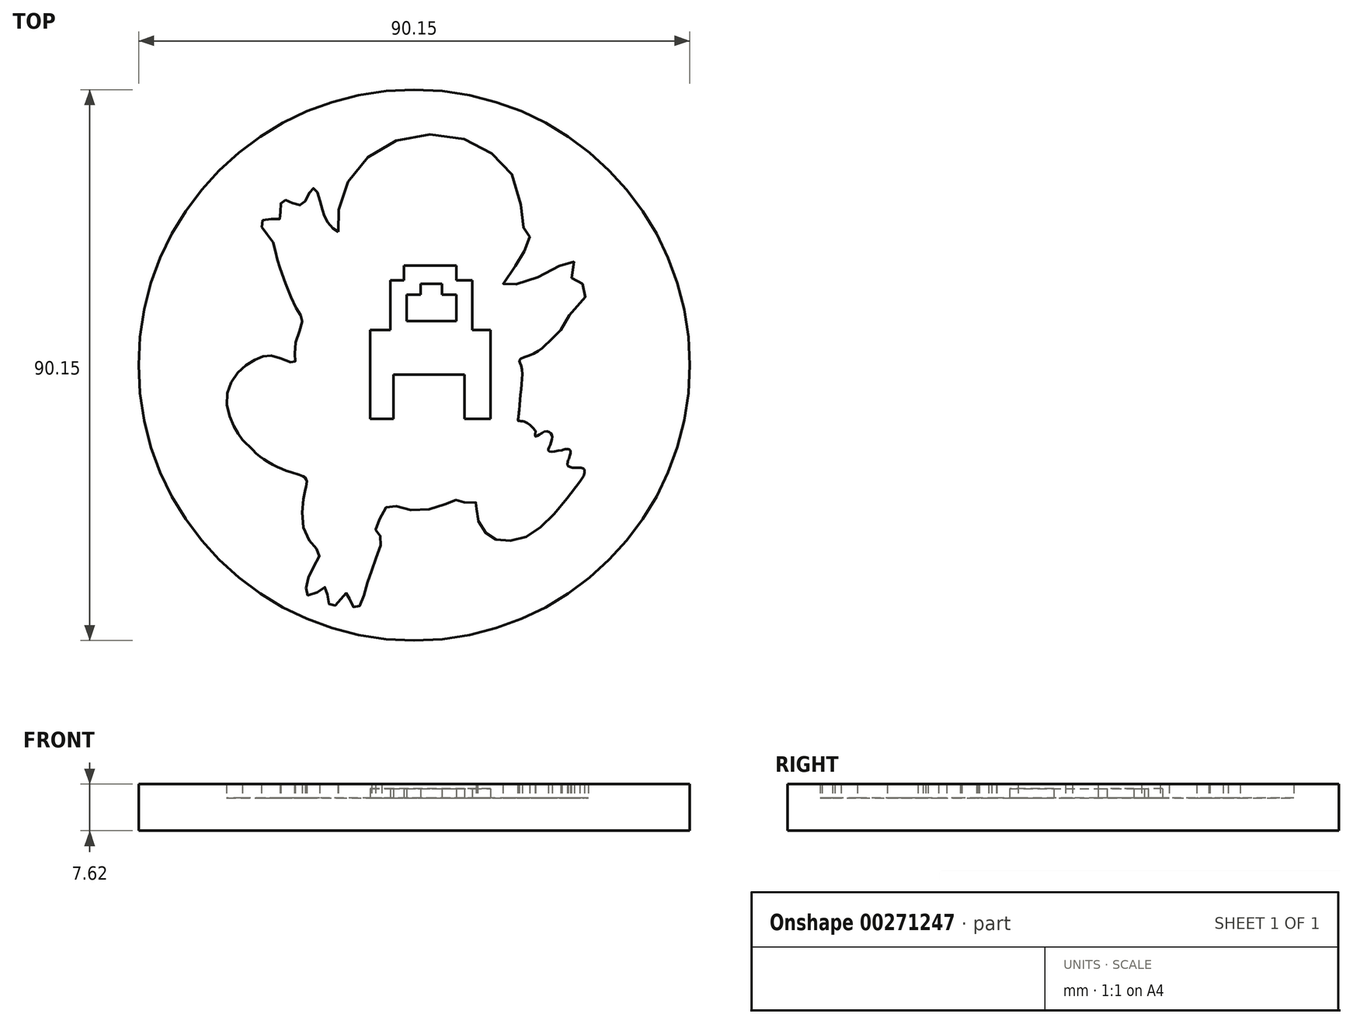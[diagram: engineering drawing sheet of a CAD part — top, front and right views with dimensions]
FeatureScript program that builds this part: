
annotation { "Feature Type Name" : "Feature", "Feature Type Description" : "" }
export const myFeature = defineFeature(function(context is Context, id is Id, definition is map)
    precondition{}
    {
        {
            var Q0;
            Q0=qCreatedBy(makeId("Top.planeOp"),FACE);
            var sketch = newSketch(context, id + "F0", { "sketchPlane" : qUnion([Q0])});
            skFitSpline(sketch, "E0", {"points": [v(-19.32, 16.1) * mm, v(-19.32, 19.22) * mm, v(-17.52, 24.62) * mm, v(-12.85, 29.53) * mm, v(-5.66, 31.93) * mm, v(2.13, 30.97) * mm, v(7.29, 27.61) * mm, v(10.28, 22.58) * mm, v(10.76, 17.07) * mm, v(11.2, 16.56) * mm, v(11.82, 15.85) * mm, v(11.96, 14.7) * mm, v(11.23, 13.16) * mm, v(10.25, 11.43) * mm, v(8.9, 9.4) * mm, v(7.6, 7.25) * mm, v(8.95, 7.25) * mm, v(12.21, 8.36) * mm, v(15.6, 9.53) * mm, v(18.49, 11.62) * mm, v(19.29, 10.94) * mm, v(18.92, 9.1) * mm, v(18.98, 7.87) * mm, v(20.52, 7.62) * mm, v(21.56, 6.4) * mm, v(19.9, 4.24) * mm, v(17.69, 1.29) * mm, v(17.07, 0) * mm], "startDerivative": vector(-5.64, 75.27) * mm, "endDerivative": vector(-18.44, -44.4) * mm});
            skFitSpline(sketch, "E1", {"points": [v(17.07, 0) * mm, v(15.3, -1.73) * mm, v(12.65, -3.84) * mm, v(10.32, -4.93) * mm, v(10.63, -5.94) * mm, v(10.63, -9.13) * mm, v(10.24, -13.1) * mm], "startDerivative": vector(-10.72, -10.36) * mm, "endDerivative": vector(-1.84, -19.44) * mm});
            skFitSpline(sketch, "E2", {"points": [v(10.24, -13.1) * mm, v(10.09, -14.52) * mm, v(10.05, -14.77) * mm, v(10.84, -14.93) * mm, v(12.08, -15.58) * mm, v(12.83, -16.38) * mm, v(12.96, -16.64) * mm], "startDerivative": vector(-0.46, -7.58) * mm, "endDerivative": vector(0.85, -2.32) * mm});
            skFitSpline(sketch, "E3", {"points": [v(12.96, -16.64) * mm, v(12.96, -17.44) * mm, v(14.36, -16.64) * mm, v(15.54, -17.04) * mm, v(15.37, -18.62) * mm, v(15.06, -19.77) * mm, v(17.23, -19.63) * mm], "startDerivative": vector(-1.66, -9.1) * mm, "endDerivative": vector(14.16, 2.9) * mm});
            skFitSpline(sketch, "E4", {"points": [v(17.23, -19.63) * mm, v(18.1, -19.46) * mm, v(18.65, -19.8) * mm, v(18.4, -20.98) * mm, v(18.15, -22) * mm, v(18.3, -22.28) * mm], "startDerivative": vector(4.13, 1.41) * mm, "endDerivative": vector(1.55, -1.87) * mm});
            skFitSpline(sketch, "E5", {"points": [v(18.3, -22.28) * mm, v(18.91, -22.51) * mm, v(20.12, -22.54) * mm, v(20.87, -22.76) * mm, v(20.79, -23.83) * mm, v(20.14, -24.8) * mm], "startDerivative": vector(3.33, -1.69) * mm, "endDerivative": vector(-3.28, -4) * mm});
            skFitSpline(sketch, "E6", {"points": [v(20.14, -24.8) * mm, v(15.28, -30.83) * mm, v(10.63, -34.1) * mm, v(6.5, -34.27) * mm, v(4.25, -32.55) * mm, v(3.22, -29.45) * mm, v(3.4, -28.33) * mm, v(1.24, -28.16) * mm, v(0, -27.82) * mm, v(-2.72, -28.85) * mm, v(-8.4, -29.28) * mm, v(-11.16, -28.76) * mm, v(-12.8, -31.43) * mm, v(-13.14, -32.98) * mm, v(-12.28, -33.93) * mm, v(-12.8, -36.25) * mm, v(-13.83, -39.35) * mm], "startDerivative": vector(-47.35, -63.76) * mm, "endDerivative": vector(-14.46, -47.3) * mm});
            skFitSpline(sketch, "E7", {"points": [v(-13.83, -39.35) * mm, v(-14.94, -42.61) * mm, v(-15.9, -45.2) * mm, v(-16.78, -45.37) * mm, v(-17.48, -43.97) * mm, v(-17.96, -43.05) * mm, v(-18.7, -43.67) * mm, v(-19.71, -44.98) * mm, v(-20.67, -45.02) * mm, v(-21.07, -43.53) * mm, v(-21.46, -42.09) * mm, v(-22.78, -42.92) * mm, v(-24.53, -43.32) * mm, v(-24.49, -41.65) * mm, v(-23.7, -39.35) * mm, v(-22.38, -36.7) * mm, v(-23.22, -35.47) * mm, v(-24.97, -32.55) * mm, v(-25.1, -28.16) * mm, v(-24.75, -26.1) * mm], "startDerivative": vector(-16.81, -44.88) * mm, "endDerivative": vector(6.7, 32.94) * mm});
            skFitSpline(sketch, "E8", {"points": [v(-24.75, -26.1) * mm, v(-24.53, -24.51) * mm, v(-25.28, -23.83) * mm, v(-26.5, -23.46) * mm, v(-31.08, -21.45) * mm, v(-34.98, -17.92) * mm], "startDerivative": vector(3.32, 11.18) * mm, "endDerivative": vector(-13.1, 13.12) * mm});
            skFitSpline(sketch, "E9", {"points": [v(-34.98, -17.92) * mm, v(-36.3, -15.94) * mm, v(-37.58, -11.32) * mm, v(-35.6, -6.77) * mm, v(-32.18, -4.5) * mm, v(-29.56, -4.36) * mm, v(-26.5, -5.28) * mm, v(-26.5, -3.06) * mm, v(-25.23, 1.5) * mm, v(-26.01, 3.23) * mm, v(-28.88, 10.14) * mm], "startDerivative": vector(-16.02, 21.1) * mm, "endDerivative": vector(-20.54, 57.47) * mm});
            skFitSpline(sketch, "E10", {"points": [v(-28.88, 10.14) * mm, v(-29.5, 12.4) * mm, v(-30.28, 14.88) * mm, v(-31.86, 16.96) * mm, v(-31.37, 18.19) * mm, v(-28.88, 18.19) * mm, v(-28.88, 20.04) * mm, v(-28.2, 21.27) * mm, v(-26.7, 20.77) * mm, v(-25.2, 20.54) * mm, v(-24.17, 22.3) * mm, v(-23.3, 23.21) * mm, v(-22.54, 21.95) * mm, v(-21.9, 19.6) * mm, v(-21.45, 18.32) * mm, v(-20.4, 16.83) * mm, v(-19.32, 16.1) * mm], "startDerivative": vector(-9.75, 30.83) * mm, "endDerivative": vector(20.83, -10.87) * mm});
            skCircle(sketch, "E11", {"center": v(-6.92, -5.72) * mm, "radius": 45.07 * mm});
            skSolve(sketch);
        }
        {
            var Q0;
            Q0=makeQuery(id+"F0.imprint","IMPRINT",FACE,{"disambiguationData":[TD([[makeQuery(id+"F0.imprint","IMPRINT",EDGE,{"derivedFrom":sQuery(id+"F0.wireOp",EDGE,"E0")}),-1.0]])]});
            extrude(context, id + "F1", {"entities" : qUnion([Q0]), "depth" : 5.33 * mm});
        }
        {
            var Q0;
            Q0=makeQuery(id+"F0.imprint","IMPRINT",FACE,{"disambiguationData":[TD([[makeQuery(id+"F0.imprint","IMPRINT",EDGE,{"derivedFrom":sQuery(id+"F0.wireOp",EDGE,"E0")}),1.0]])]});
            extrude(context, id + "F2", {"entities" : qUnion([Q0]), "operationType" : NewBodyOperationType.ADD, "depth" : 7.62 * mm});
        }
        {
            var Q0;
            Q0=makeQuery(id+"F1.opExtrude","CAP_FACE",FACE,{"disambiguationData":[OSD([sQuery(id+"F0.wireOp",EDGE,"E0"),sQuery(id+"F0.wireOp",EDGE,"E1"),sQuery(id+"F0.wireOp",EDGE,"E2"),sQuery(id+"F0.wireOp",EDGE,"E3"),sQuery(id+"F0.wireOp",EDGE,"E4"),sQuery(id+"F0.wireOp",EDGE,"E5"),sQuery(id+"F0.wireOp",EDGE,"E6"),sQuery(id+"F0.wireOp",EDGE,"E7"),sQuery(id+"F0.wireOp",EDGE,"E8"),sQuery(id+"F0.wireOp",EDGE,"E9"),sQuery(id+"F0.wireOp",EDGE,"E10")])],"isStart":false});
            var sketch = newSketch(context, id + "F3", { "sketchPlane" : qUnion([Q0])});
            skLineSegment(sketch, "E12", {"start": v(0, 10.54) * mm, "end": v(0, 8.17) * mm});
            skLineSegment(sketch, "E13", {"start": v(0, 8.17) * mm, "end": v(2.6, 8.17) * mm});
            skLineSegment(sketch, "E14", {"start": v(2.6, 8.17) * mm, "end": v(2.6, 0) * mm});
            skLineSegment(sketch, "E15", {"start": v(2.6, 0) * mm, "end": v(5.6, 0) * mm});
            skLineSegment(sketch, "E16", {"start": v(5.6, 0) * mm, "end": v(5.6, -14.51) * mm});
            skLineSegment(sketch, "E17", {"start": v(5.6, -14.51) * mm, "end": v(1.34, -14.51) * mm});
            skLineSegment(sketch, "E18", {"start": v(1.34, -14.51) * mm, "end": v(1.34, -7.27) * mm});
            skLineSegment(sketch, "E19", {"start": v(1.34, -7.27) * mm, "end": v(-10.31, -7.27) * mm});
            skLineSegment(sketch, "E20", {"start": v(-10.31, -7.27) * mm, "end": v(-10.31, -14.51) * mm});
            skLineSegment(sketch, "E21", {"start": v(-10.31, -14.51) * mm, "end": v(-14.1, -14.51) * mm});
            skLineSegment(sketch, "E22", {"start": v(-14.1, -14.51) * mm, "end": v(-14.1, 0) * mm});
            skLineSegment(sketch, "E23", {"start": v(-14.1, 0) * mm, "end": v(-10.79, 0) * mm});
            skLineSegment(sketch, "E24", {"start": v(-10.79, 0) * mm, "end": v(-10.79, 8.17) * mm});
            skLineSegment(sketch, "E25", {"start": v(-10.79, 8.17) * mm, "end": v(-8.59, 8.17) * mm});
            skLineSegment(sketch, "E26", {"start": v(-8.59, 8.17) * mm, "end": v(-8.59, 10.54) * mm});
            skLineSegment(sketch, "E27", {"start": v(-8.59, 10.54) * mm, "end": v(0, 10.54) * mm});
            skLineSegment(sketch, "E28.bottom", {"start": v(-8.16, 5.8) * mm, "end": v(-5.86, 5.8) * mm});
            skLineSegment(sketch, "E28.top", {"start": v(-8.16, 1.47) * mm, "end": v(0, 1.47) * mm});
            skLineSegment(sketch, "E28.left", {"start": v(-8.16, 5.8) * mm, "end": v(-8.16, 1.47) * mm});
            skLineSegment(sketch, "E28.right", {"start": v(0, 5.8) * mm, "end": v(0, 1.47) * mm});
            skLineSegment(sketch, "E29.top", {"start": v(-5.86, 7.55) * mm, "end": v(-2.36, 7.55) * mm});
            skLineSegment(sketch, "E29.left", {"start": v(-5.86, 5.8) * mm, "end": v(-5.86, 7.55) * mm});
            skLineSegment(sketch, "E29.right", {"start": v(-2.36, 5.8) * mm, "end": v(-2.36, 7.55) * mm});
            skLineSegment(sketch, "E30.trimOffspring", {"start": v(-2.36, 5.8) * mm, "end": v(0, 5.8) * mm});
            skSolve(sketch);
        }
        {
            var Q0;
            Q0=makeQuery(id+"F3.imprint","IMPRINT",FACE,{"disambiguationData":[TD([[makeQuery(id+"F3.imprint","IMPRINT",EDGE,{"derivedFrom":sQuery(id+"F3.wireOp",EDGE,"E12")}),-1.0]])]});
            extrude(context, id + "F4", {"entities" : qUnion([Q0]), "operationType" : NewBodyOperationType.ADD, "depth" : 1.52 * mm});
        }
    });
